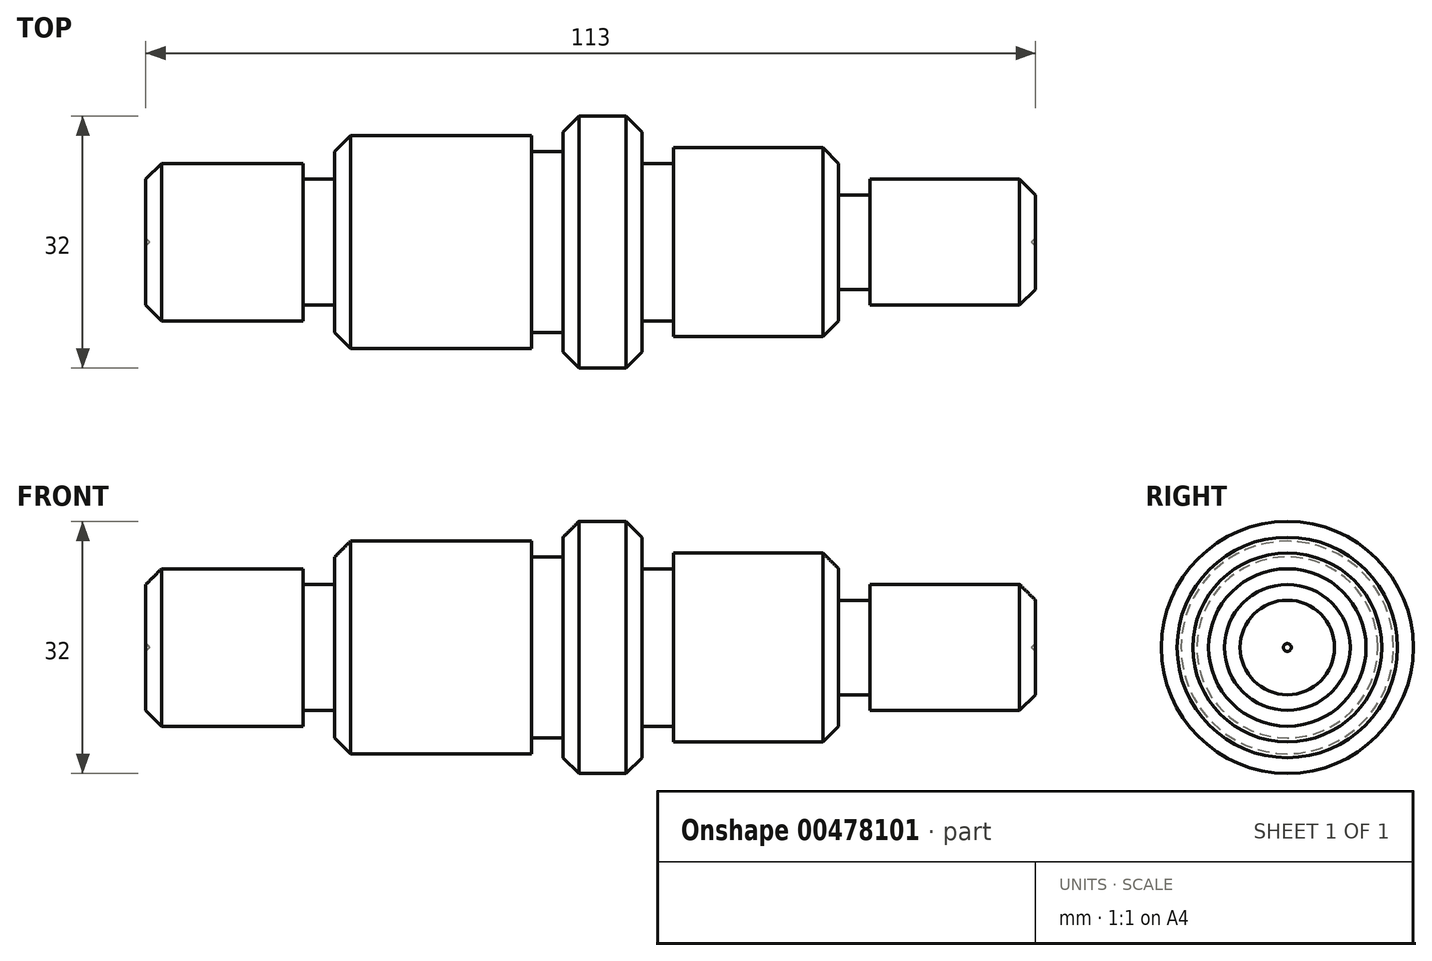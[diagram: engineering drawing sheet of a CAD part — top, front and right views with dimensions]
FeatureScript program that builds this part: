
annotation { "Feature Type Name" : "Feature", "Feature Type Description" : "" }
export const myFeature = defineFeature(function(context is Context, id is Id, definition is map)
    precondition{}
    {
        {
            var Q0;
            Q0=qCreatedBy(makeId("Top.planeOp"),FACE);
            var sketch = newSketch(context, id + "F0", { "sketchPlane" : qUnion([Q0])});
            skLineSegment(sketch, "E0.bottom", {"start": v(0, 0) * mm, "end": v(20, 0) * mm});
            skLineSegment(sketch, "E0.top", {"start": v(0, -10) * mm, "end": v(20, -10) * mm});
            skLineSegment(sketch, "E0.left", {"start": v(0, 0) * mm, "end": v(0, -10) * mm});
            skLineSegment(sketch, "E0.right", {"start": v(20, 0) * mm, "end": v(20, -10) * mm});
            skLineSegment(sketch, "E1.bottom", {"start": v(20, 0) * mm, "end": v(24, 0) * mm});
            skLineSegment(sketch, "E1.top", {"start": v(20, -8) * mm, "end": v(24, -8) * mm});
            skLineSegment(sketch, "E1.left", {"start": v(20, 0) * mm, "end": v(20, -8) * mm});
            skLineSegment(sketch, "E1.right", {"start": v(24, 0) * mm, "end": v(24, -8) * mm});
            skLineSegment(sketch, "E2.bottom", {"start": v(24, 0) * mm, "end": v(53, 0) * mm});
            skLineSegment(sketch, "E2.top", {"start": v(24, -13.5) * mm, "end": v(53, -13.5) * mm});
            skLineSegment(sketch, "E2.left", {"start": v(24, 0) * mm, "end": v(24, -13.5) * mm});
            skLineSegment(sketch, "E2.right", {"start": v(53, 0) * mm, "end": v(53, -13.5) * mm});
            skLineSegment(sketch, "E3.bottom", {"start": v(53, 0) * mm, "end": v(63, 0) * mm});
            skLineSegment(sketch, "E3.top", {"start": v(53, -16) * mm, "end": v(63, -16) * mm});
            skLineSegment(sketch, "E3.left", {"start": v(53, 0) * mm, "end": v(53, -16) * mm});
            skLineSegment(sketch, "E3.right", {"start": v(63, 0) * mm, "end": v(63, -16) * mm});
            skLineSegment(sketch, "E4.bottom", {"start": v(63, 0) * mm, "end": v(67, 0) * mm});
            skLineSegment(sketch, "E4.top", {"start": v(63, -10) * mm, "end": v(67, -10) * mm});
            skLineSegment(sketch, "E4.left", {"start": v(63, 0) * mm, "end": v(63, -10) * mm});
            skLineSegment(sketch, "E4.right", {"start": v(67, 0) * mm, "end": v(67, -10) * mm});
            skLineSegment(sketch, "E5.bottom", {"start": v(67, 0) * mm, "end": v(88, 0) * mm});
            skLineSegment(sketch, "E5.top", {"start": v(67, -12) * mm, "end": v(88, -12) * mm});
            skLineSegment(sketch, "E5.left", {"start": v(67, 0) * mm, "end": v(67, -12) * mm});
            skLineSegment(sketch, "E5.right", {"start": v(88, 0) * mm, "end": v(88, -12) * mm});
            skLineSegment(sketch, "E6.bottom", {"start": v(88, 0) * mm, "end": v(92, 0) * mm});
            skLineSegment(sketch, "E6.top", {"start": v(88, -6) * mm, "end": v(92, -6) * mm});
            skLineSegment(sketch, "E6.left", {"start": v(88, 0) * mm, "end": v(88, -6) * mm});
            skLineSegment(sketch, "E6.right", {"start": v(92, 0) * mm, "end": v(92, -6) * mm});
            skLineSegment(sketch, "E7.bottom", {"start": v(92, 0) * mm, "end": v(113, 0) * mm});
            skLineSegment(sketch, "E7.top", {"start": v(92, -8) * mm, "end": v(113, -8) * mm});
            skLineSegment(sketch, "E7.left", {"start": v(92, 0) * mm, "end": v(92, -8) * mm});
            skLineSegment(sketch, "E7.right", {"start": v(113, 0) * mm, "end": v(113, -8) * mm});
            skLineSegment(sketch, "E8.bottom", {"start": v(53, 0) * mm, "end": v(49, 0) * mm});
            skLineSegment(sketch, "E8.top", {"start": v(53, -11.5) * mm, "end": v(49, -11.5) * mm});
            skLineSegment(sketch, "E8.left", {"start": v(53, 0) * mm, "end": v(53, -11.5) * mm});
            skLineSegment(sketch, "E8.right", {"start": v(49, 0) * mm, "end": v(49, -11.5) * mm, "construction": true});
            skLineSegment(sketch, "E9.bottom", {"start": v(49, -11.5) * mm, "end": v(53, -11.5) * mm});
            skLineSegment(sketch, "E9.top", {"start": v(49, -13.5) * mm, "end": v(53, -13.5) * mm});
            skLineSegment(sketch, "E9.left", {"start": v(49, -11.5) * mm, "end": v(49, -13.5) * mm});
            skLineSegment(sketch, "E9.right", {"start": v(53, -11.5) * mm, "end": v(53, -13.5) * mm});
            skLineSegment(sketch, "E10", {"start": v(0, -0.5) * mm, "end": v(0.5, 0) * mm});
            skLineSegment(sketch, "E11", {"start": v(113, -0.5) * mm, "end": v(112.5, 0) * mm});
            skSolve(sketch);
        }
        {
            var Q0;
            {var subQ3=sQuery(id+"F0.wireOp",EDGE,"E2.bottom");Q0=makeQuery(id+"F0.imprint","IMPRINT",FACE,{"disambiguationData":[TD([[makeQuery(id+"F0.imprint","IMPRINT",EDGE,{"derivedFrom":subQ3}),-1.0]])]});}
            var Q1;
            {var subQ3=sQuery(id+"F0.wireOp",EDGE,"E3.bottom");Q1=makeQuery(id+"F0.imprint","IMPRINT",FACE,{"disambiguationData":[TD([[makeQuery(id+"F0.imprint","IMPRINT",EDGE,{"derivedFrom":subQ3}),-1.0]])]});}
            var Q2;
            {var subQ0=sQuery(id+"F0.wireOp",EDGE,"E1.bottom");Q2=makeQuery(id+"F0.imprint","IMPRINT",FACE,{"disambiguationData":[TD([[makeQuery(id+"F0.imprint","IMPRINT",EDGE,{"derivedFrom":subQ0}),-1.0]])]});}
            var Q3;
            {var subQ0=sQuery(id+"F0.wireOp",EDGE,"E4.bottom");Q3=makeQuery(id+"F0.imprint","IMPRINT",FACE,{"disambiguationData":[TD([[makeQuery(id+"F0.imprint","IMPRINT",EDGE,{"derivedFrom":subQ0}),-1.0]])]});}
            var Q4;
            {var subQ3=sQuery(id+"F0.wireOp",EDGE,"E5.bottom");Q4=makeQuery(id+"F0.imprint","IMPRINT",FACE,{"disambiguationData":[TD([[makeQuery(id+"F0.imprint","IMPRINT",EDGE,{"derivedFrom":subQ3}),-1.0]])]});}
            var Q5;
            {var subQ0=sQuery(id+"F0.wireOp",EDGE,"E6.bottom");Q5=makeQuery(id+"F0.imprint","IMPRINT",FACE,{"disambiguationData":[TD([[makeQuery(id+"F0.imprint","IMPRINT",EDGE,{"derivedFrom":subQ0}),-1.0]])]});}
            var Q6;
            {var subQ1=sQuery(id+"F0.wireOp",EDGE,"E0.top");Q6=makeQuery(id+"F0.imprint","IMPRINT",FACE,{"disambiguationData":[TD([[makeQuery(id+"F0.imprint","IMPRINT",EDGE,{"derivedFrom":subQ1}),1.0]])]});}
            var Q7;
            {var subQ2=sQuery(id+"F0.wireOp",EDGE,"E7.top");Q7=makeQuery(id+"F0.imprint","IMPRINT",FACE,{"disambiguationData":[TD([[makeQuery(id+"F0.imprint","IMPRINT",EDGE,{"derivedFrom":subQ2}),1.0]])]});}
            var Q8;
            Q8=sQuery(id+"F0.wireOp",EDGE,"E0.bottom");
            revolve(context, id + "F1", {"entities" : qUnion([Q0, Q1, Q2, Q3, Q4, Q5, Q6, Q7]), "axis" : qUnion([Q8]), "revolveType" : RevolveType.FULL});
        }
        {
            var Q0;
            Q0=makeQuery(id+"F1.opRevolve","SWEPT_EDGE",EDGE,{"disambiguationData":[OSD([sQuery(id+"F0.wireOp",EDGE,"E0.top"),sQuery(id+"F0.wireOp",EDGE,"E0.left")])]});
            var Q1;
            Q1=makeQuery(id+"F1.opRevolve","SWEPT_EDGE",EDGE,{"disambiguationData":[OSD([sQuery(id+"F0.wireOp",EDGE,"E2.top"),sQuery(id+"F0.wireOp",EDGE,"E2.left")])]});
            var Q2;
            Q2=makeQuery(id+"F1.opRevolve","SWEPT_EDGE",EDGE,{"disambiguationData":[OSD([sQuery(id+"F0.wireOp",EDGE,"E3.top"),sQuery(id+"F0.wireOp",EDGE,"E3.left")])]});
            var Q3;
            Q3=makeQuery(id+"F1.opRevolve","SWEPT_EDGE",EDGE,{"disambiguationData":[OSD([sQuery(id+"F0.wireOp",EDGE,"E3.top"),sQuery(id+"F0.wireOp",EDGE,"E3.right")])]});
            var Q4;
            Q4=makeQuery(id+"F1.opRevolve","SWEPT_EDGE",EDGE,{"disambiguationData":[OSD([sQuery(id+"F0.wireOp",EDGE,"E5.top"),sQuery(id+"F0.wireOp",EDGE,"E5.right")])]});
            var Q5;
            Q5=makeQuery(id+"F1.opRevolve","SWEPT_EDGE",EDGE,{"disambiguationData":[OSD([sQuery(id+"F0.wireOp",EDGE,"E7.top"),sQuery(id+"F0.wireOp",EDGE,"E7.right")])]});
            chamfer(context, id + "F2", {"entities" : qUnion([Q0, Q1, Q2, Q3, Q4, Q5]), "width" : 2 * mm, "tangentPropagation" : true});
        }
    });
